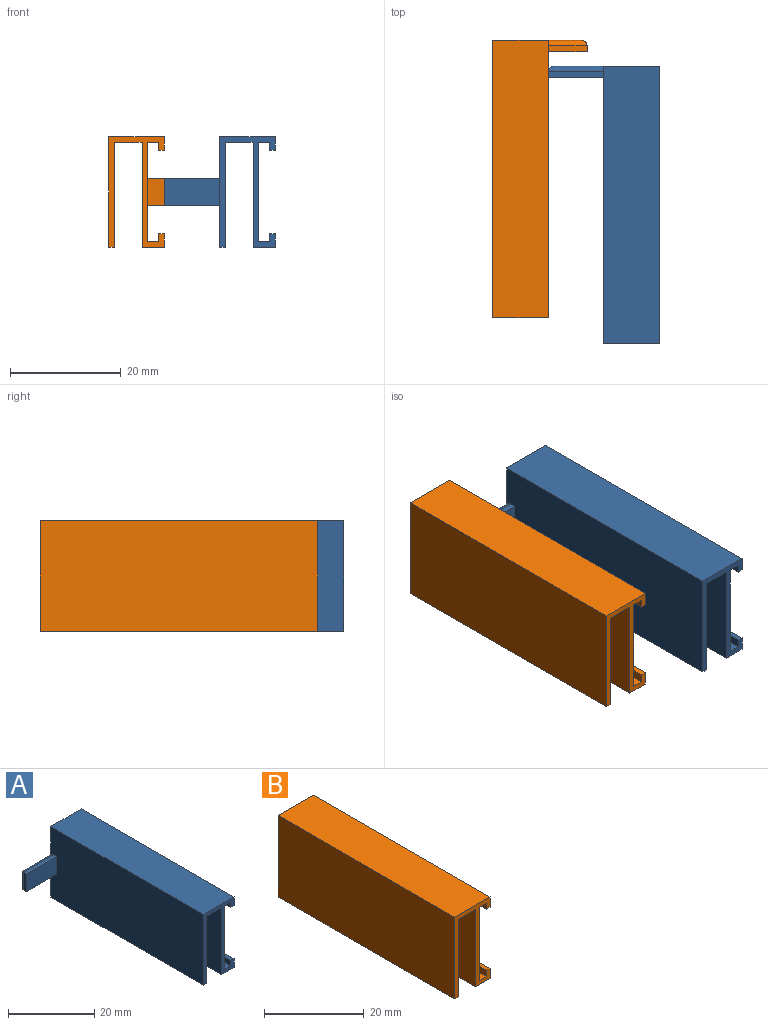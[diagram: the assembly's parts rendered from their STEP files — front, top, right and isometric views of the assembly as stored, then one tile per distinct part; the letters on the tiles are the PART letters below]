
ASSEMBLY  parts=2 mates=1
PART A: 25 faces, bbox 20x50x20 mm
  f0: plane 20x10mm, normal (0,-1,0), area 54mm2, adj f2,f3,f4,f5,f6,f7,f8,f9
  f1: plane 20x19mm, normal (0,1,0), area 81mm2, adj f2,f3,f4,f5,f6,f7,f8,f9
  f2: plane 50x1mm, normal (0,0,-1), area 50mm2, adj f0,f1,f5,f17
  f3: plane 50x18mm, normal (1,0,0), area 900mm2, adj f0,f1,f7,f8
  f4: plane 50x10mm, normal (0,0,1), area 500mm2, adj f0,f1,f5,f11
  f5: plane 50x20mm, normal (-1,0,0), area 990.4mm2, adj f0,f1,f2,f4,f18,f19,f20,f22
  f6: plane 50x4mm, normal (0,0,-1), area 200mm2, adj f0,f1,f13,f15
  f7: plane 50x2mm, normal (0,0,-1), area 100mm2, adj f0,f1,f3,f9
  f8: plane 50x2mm, normal (0,0,1), area 100mm2, adj f0,f1,f3,f14
  f9: plane 50x1.5mm, normal (-1,0,0), area 75mm2, adj f0,f1,f7,f10
  f10: plane 50x1mm, normal (0,0,-1), area 50mm2, adj f0,f1,f9,f11
  f11: plane 50x2.5mm, normal (1,0,0), area 125mm2, adj f0,f1,f4,f10
  f12: plane 50x1mm, normal (0,0,1), area 50mm2, adj f0,f1,f13,f14
  f13: plane 50x2.5mm, normal (1,0,0), area 125mm2, adj f0,f1,f6,f12
  f14: plane 50x1.5mm, normal (-1,0,0), area 75mm2, adj f0,f1,f8,f12
  f15: plane 50x19mm, normal (-1,0,0), area 950mm2, adj f0,f1,f6,f16
  f16: plane 50x5mm, normal (0,0,-1), area 250mm2, adj f0,f1,f15,f17
  f17: plane 50x19mm, normal (1,0,0), area 950mm2, adj f0,f1,f2,f16
  f18: plane 10x1mm, normal (0,0,1), area 10mm2, adj f5,f19,f21,f24
  f19: plane 10x5mm, normal (0,-1,0), area 50mm2, adj f5,f18,f20,f21
  f20: plane 10x1mm, normal (0,0,-1), area 10mm2, adj f5,f19,f21,f22
  f21: plane 5x1mm, normal (-1,0,0), area 5mm2, adj f18,f19,f20,f23
  f22: cylinder r=1mm len=10mm, axis (1,0,0), area 15.1mm2, adj f1,f5,f20,f23
  f23: cylinder r=1mm len=5mm, axis (0,0,-1), area 6.7mm2, adj f1,f21,f22,f24
  f24: cylinder r=1mm len=10mm, axis (-1,0,0), area 15.1mm2, adj f1,f5,f18,f23
PART B: 25 faces, bbox 17x50x20 mm
  f0: plane 50x18mm, normal (1,0,0), area 890.4mm2, adj f1,f2,f7,f8,f18,f19,f20,f22
  f1: plane 20x10mm, normal (0,-1,0), area 54mm2, adj f0,f3,f4,f5,f6,f7,f8,f9
  f2: plane 20x16mm, normal (0,1,0), area 81mm2, adj f0,f3,f4,f5,f6,f7,f8,f9
  f3: plane 50x1mm, normal (0,0,-1), area 50mm2, adj f1,f2,f5,f17
  f4: plane 50x10mm, normal (0,0,1), area 500mm2, adj f1,f2,f5,f11
  f5: plane 50x20mm, normal (-1,0,0), area 1000mm2, adj f1,f2,f3,f4
  f6: plane 50x4mm, normal (0,0,-1), area 200mm2, adj f1,f2,f13,f15
  f7: plane 50x2mm, normal (0,0,-1), area 100mm2, adj f0,f1,f2,f9
  f8: plane 50x2mm, normal (0,0,1), area 100mm2, adj f0,f1,f2,f14
  f9: plane 50x1.5mm, normal (-1,0,0), area 75mm2, adj f1,f2,f7,f10
  f10: plane 50x1mm, normal (0,0,-1), area 50mm2, adj f1,f2,f9,f11
  f11: plane 50x2.5mm, normal (1,0,0), area 125mm2, adj f1,f2,f4,f10
  f12: plane 50x1mm, normal (0,0,1), area 50mm2, adj f1,f2,f13,f14
  f13: plane 50x2.5mm, normal (1,0,0), area 125mm2, adj f1,f2,f6,f12
  f14: plane 50x1.5mm, normal (-1,0,0), area 75mm2, adj f1,f2,f8,f12
  f15: plane 50x19mm, normal (-1,0,0), area 950mm2, adj f1,f2,f6,f16
  f16: plane 50x5mm, normal (0,0,-1), area 250mm2, adj f1,f2,f15,f17
  f17: plane 50x19mm, normal (1,0,0), area 950mm2, adj f1,f2,f3,f16
  f18: plane 10x1mm, normal (0,0,1), area 10mm2, adj f0,f19,f21,f22
  f19: plane 10x5mm, normal (0,-1,0), area 50mm2, adj f0,f18,f20,f21
  f20: plane 10x1mm, normal (0,0,-1), area 10mm2, adj f0,f19,f21,f24
  f21: plane 5x1mm, normal (1,0,0), area 5mm2, adj f18,f19,f20,f23
  f22: cylinder r=1mm len=10mm, axis (1,0,0), area 15.1mm2, adj f0,f2,f18,f23
  f23: cylinder r=1mm len=5mm, axis (0,0,1), area 6.7mm2, adj f2,f21,f22,f24
  f24: cylinder r=1mm len=10mm, axis (-1,0,0), area 15.1mm2, adj f0,f2,f20,f23
PLACE A t=(-3.5,50.66,0)mm
PLACE B t=(-23.5,55.28,0)mm
MATE parallel B.f5 <-> A.f5  axis (-1,0,0) through (-27,30.28,0)mm
